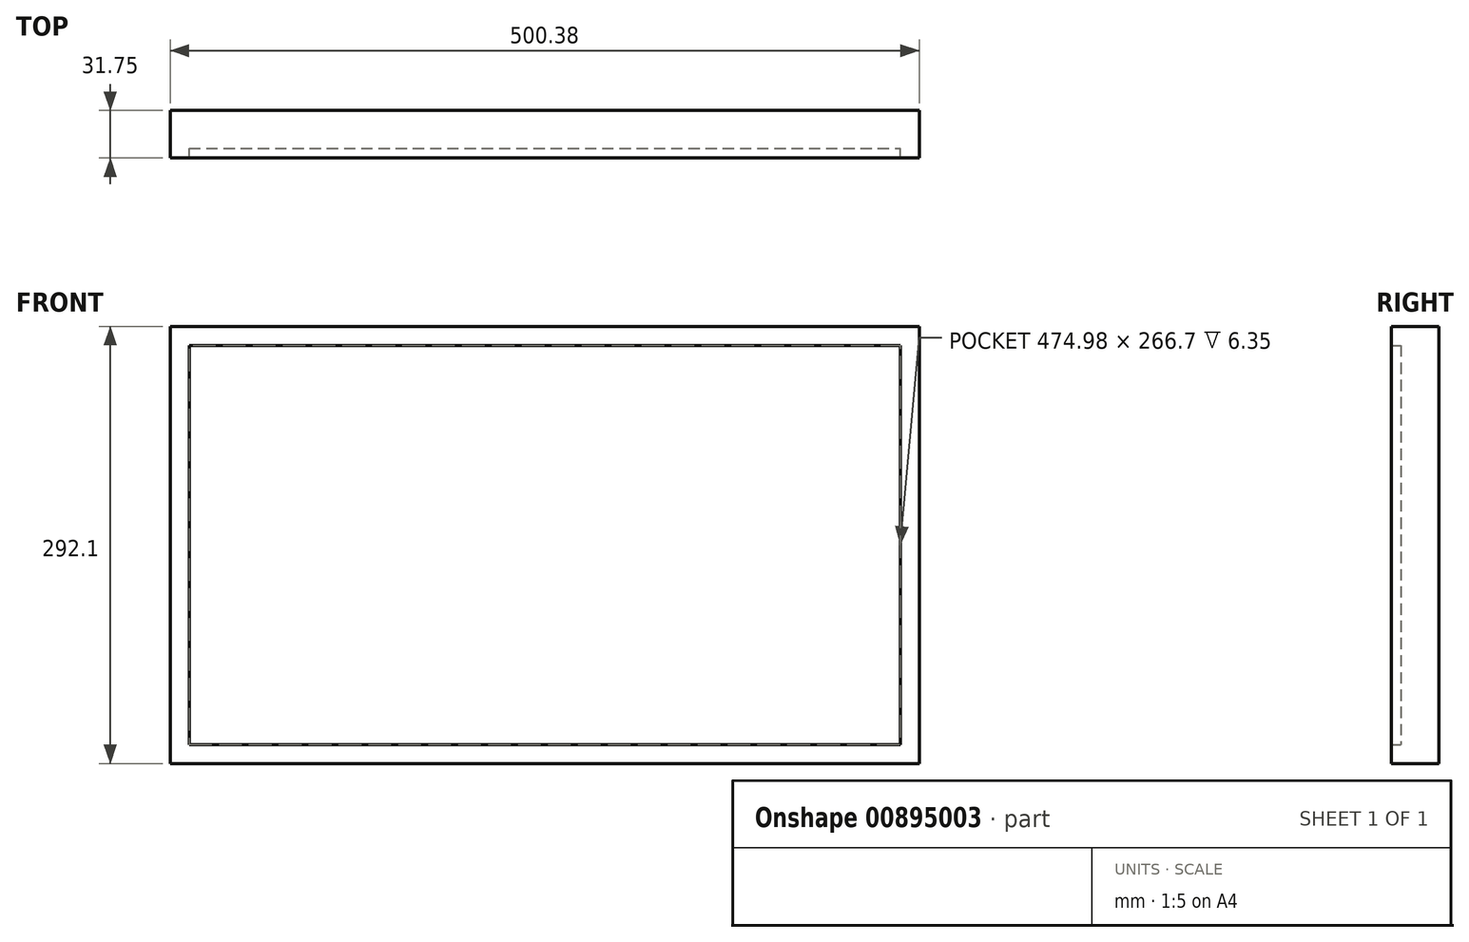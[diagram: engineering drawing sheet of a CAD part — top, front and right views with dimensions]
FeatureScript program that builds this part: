
annotation { "Feature Type Name" : "Feature", "Feature Type Description" : "" }
export const myFeature = defineFeature(function(context is Context, id is Id, definition is map)
    precondition{}
    {
        {
            var Q0;
            Q0=qCreatedBy(makeId("Front.planeOp"),FACE);
            var sketch = newSketch(context, id + "F0", { "sketchPlane" : qUnion([Q0])});
            skLineSegment(sketch, "E0.bottom", {"start": v(-237.49, 133.35) * mm, "end": v(237.5, 133.35) * mm});
            skLineSegment(sketch, "E0.top", {"start": v(-237.49, -133.35) * mm, "end": v(237.49, -133.35) * mm});
            skLineSegment(sketch, "E0.left", {"start": v(-237.49, 133.35) * mm, "end": v(-237.5, -133.35) * mm});
            skLineSegment(sketch, "E0.right", {"start": v(237.5, 133.35) * mm, "end": v(237.49, -133.35) * mm});
            skPoint(sketch, "E0.middle", {"position": v(0, 0) * mm});
            skSolve(sketch);
        }
        {
            var Q0;
            Q0=makeQuery(id+"F0.imprint","IMPRINT",FACE,{"disambiguationData":[TD([[makeQuery(id+"F0.imprint","IMPRINT",EDGE,{"derivedFrom":sQuery(id+"F0.wireOp",EDGE,"E0.bottom")}),-1.0]])]});
            extrude(context, id + "F1", {"entities" : qUnion([Q0]), "depth" : 25.4 * mm, "offsetDistance" : 25.4 * mm});
        }
        {
            var Q0;
            Q0=qCreatedBy(makeId("Front.planeOp"),FACE);
            var sketch = newSketch(context, id + "F2", { "sketchPlane" : qUnion([Q0])});
            skLineSegment(sketch, "E1.bottom", {"start": v(-250.2, 146.05) * mm, "end": v(250.2, 146.05) * mm});
            skLineSegment(sketch, "E1.top", {"start": v(-250.2, -146.05) * mm, "end": v(250.2, -146.05) * mm});
            skLineSegment(sketch, "E1.left", {"start": v(-250.19, 146.05) * mm, "end": v(-250.19, -146.05) * mm});
            skLineSegment(sketch, "E1.right", {"start": v(250.19, 146.05) * mm, "end": v(250.19, -146.05) * mm});
            skPoint(sketch, "E1.middle", {"position": v(0, 0) * mm});
            skLineSegment(sketch, "E2.0.0", {"start": v(237.5, 133.35) * mm, "end": v(-237.49, 133.35) * mm});
            skLineSegment(sketch, "E2.0.1", {"start": v(-237.49, 133.35) * mm, "end": v(-237.5, -133.35) * mm});
            skLineSegment(sketch, "E2.0.2", {"start": v(-237.49, -133.35) * mm, "end": v(237.49, -133.35) * mm});
            skLineSegment(sketch, "E2.0.3", {"start": v(237.49, -133.35) * mm, "end": v(237.5, 133.35) * mm});
            skSolve(sketch);
        }
        {
            var Q0;
            Q0 = qSketchRegion(id + "F2", true);
            extrude(context, id + "F3", {"entities" : qUnion([Q0]), "operationType" : NewBodyOperationType.ADD, "depth" : 31.75 * mm, "offsetDistance" : 25.4 * mm});
        }
    });
